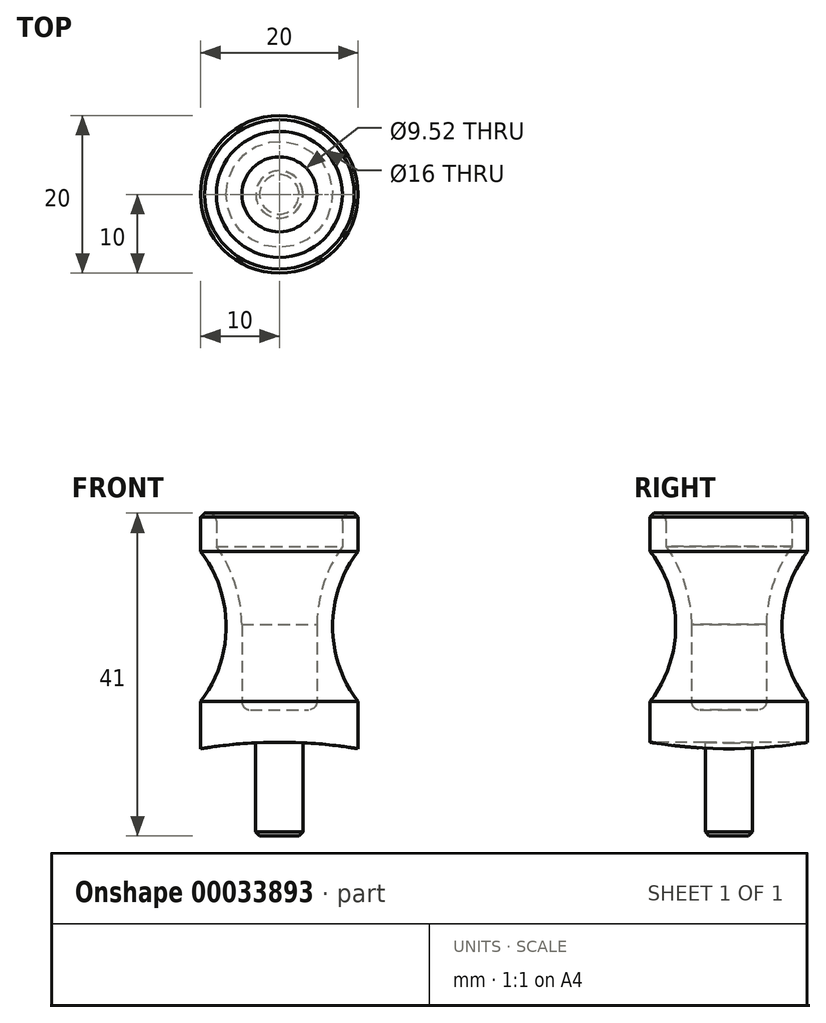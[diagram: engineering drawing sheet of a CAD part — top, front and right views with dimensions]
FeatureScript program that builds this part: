
annotation { "Feature Type Name" : "Feature", "Feature Type Description" : "" }
export const myFeature = defineFeature(function(context is Context, id is Id, definition is map)
    precondition{}
    {
        {
            var Q0;
            Q0=qCreatedBy(makeId("Front.planeOp"),FACE);
            var sketch = newSketch(context, id + "F0", { "sketchPlane" : qUnion([Q0])});
            skLineSegment(sketch, "E0", {"start": v(0, 0.9) * mm, "end": v(0, 63.05) * mm});
            skLineSegment(sketch, "E1", {"start": v(0, 0) * mm, "end": v(-10, 0) * mm});
            skLineSegment(sketch, "E2.0", {"start": v(-9, 30) * mm, "end": v(-10, 30) * mm});
            skLineSegment(sketch, "E3.0", {"start": v(-10, 0) * mm, "end": v(-10, 6.06) * mm});
            skArc(sketch, "E4.trimOffspring", {"start": v(-10, 6.06) * mm, "mid": v(-6.76, 15.6) * mm, "end": v(-10, 25.13) * mm});
            skLineSegment(sketch, "E5.trimOffspring", {"start": v(-10, 25.13) * mm, "end": v(-10, 30) * mm});
            skLineSegment(sketch, "E6.0", {"start": v(-8, 25.79) * mm, "end": v(-8, 29) * mm});
            skArc(sketch, "E7.0", {"start": v(-4.76, 15.35) * mm, "mid": v(-5.55, 20.82) * mm, "end": v(-8, 25.79) * mm});
            skLineSegment(sketch, "E8.0", {"start": v(0, 5) * mm, "end": v(-3.7, 5) * mm});
            skLineSegment(sketch, "E9.0", {"start": v(0, -60) * mm, "end": v(-10, -60) * mm});
            skArc(sketch, "E10", {"start": v(10, 0.07) * mm, "mid": v(0, 0.9) * mm, "end": v(-10, 0.07) * mm});
            skLineSegment(sketch, "E11.MirrorCS", {"start": v(10, 0) * mm, "end": v(10, 6.06) * mm});
            skLineSegment(sketch, "E12", {"start": v(0, 0) * mm, "end": v(0, 0.9) * mm});
            skLineSegment(sketch, "E13", {"start": v(0, 0) * mm, "end": v(10, 0) * mm});
            skLineSegment(sketch, "E14", {"start": v(-4.76, 15.84) * mm, "end": v(-4.76, 6.07) * mm});
            skPoint(sketch, "E14.startSnap0", {"position": v(-4.76, 15.35) * mm});
            skPoint(sketch, "E15.visualSharp", {"position": v(-4.76, 5) * mm});
            skArc(sketch, "E15.filletArc", {"start": v(-4.76, 6.07) * mm, "mid": v(-4.45, 5.31) * mm, "end": v(-3.7, 5) * mm});
            skPoint(sketch, "E16.visualSharp", {"position": v(-8, 30) * mm});
            skArc(sketch, "E16.filletArc", {"start": v(-8, 29) * mm, "mid": v(-8.3, 29.7) * mm, "end": v(-9, 30) * mm});
            skSolve(sketch);
        }
        {
            var Q0;
            {var subQ1=sQuery(id+"F0.wireOp",EDGE,"E1");Q0=makeQuery(id+"F0.imprint","IMPRINT",FACE,{"disambiguationData":[TD([[makeQuery(id+"F0.imprint","IMPRINT",EDGE,{"derivedFrom":subQ1}),-1.0]])]});}
            var Q1;
            Q1=makeQuery(id+"F0.imprint","IMPRINT",FACE,{"disambiguationData":[TD([[makeQuery(id+"F0.imprint","IMPRINT",EDGE,{"derivedFrom":sQuery(id+"F0.wireOp",EDGE,"E2.0")}),1.0]])]});
            var Q2;
            Q2=sQuery(id+"F0.wireOp",EDGE,"E10");
            var Q3;
            Q3=sQuery(id+"F0.wireOp",EDGE,"E0");
            revolve(context, id + "F1", {"entities" : qUnion([Q0, Q1]), "surfaceEntities" : qUnion([Q2]), "axis" : qUnion([Q3]), "revolveType" : RevolveType.FULL});
        }
        {
            var Q0;
            {var subQ4=sQuery(id+"F0.wireOp",EDGE,"E1");Q0=makeQuery(id+"F0.imprint","IMPRINT",FACE,{"disambiguationData":[TD([[makeQuery(id+"F0.imprint","IMPRINT",EDGE,{"derivedFrom":subQ4}),-1.0]])]});}
            var Q1;
            {var subQ1=sQuery(id+"F0.wireOp",EDGE,"E12");Q1=makeQuery(id+"F0.imprint","IMPRINT",FACE,{"disambiguationData":[TD([[makeQuery(id+"F0.imprint","IMPRINT",EDGE,{"derivedFrom":subQ1}),-1.0]])]});}
            extrude(context, id + "F2", {"entities" : qUnion([Q0, Q1]), "operationType" : NewBodyOperationType.REMOVE, "endBound" : BoundingType.SYMMETRIC, "oppositeDirection" : true, "depth" : 25 * mm});
        }
        {
            var Q0;
            Q0=makeQuery(id+"F1.opRevolve","SWEPT_FACE",FACE,{"disambiguationData":[OSD([sQuery(id+"F0.wireOp",EDGE,"E8.0")])]});
            var sketch = newSketch(context, id + "F3", { "sketchPlane" : qUnion([Q0])});
            skCircle(sketch, "E17", {"center": v(0, 0) * mm, "radius": 3 * mm});
            skSolve(sketch);
        }
        {
            var Q0;
            Q0 = qSketchRegion(id + "F3", true);
            extrude(context, id + "F4", {"entities" : qUnion([Q0]), "operationType" : NewBodyOperationType.ADD, "oppositeDirection" : true, "depth" : 16 * mm});
        }
        {
            var Q0;
            Q0=makeQuery(id+"F1.opRevolve","SWEPT_EDGE",EDGE,{"disambiguationData":[OSD([sQuery(id+"F0.wireOp",EDGE,"E2.0"),sQuery(id+"F0.wireOp",EDGE,"E5.trimOffspring")])]});
            chamfer(context, id + "F5", {"entities" : qUnion([Q0]), "width" : 0.5 * mm, "tangentPropagation" : true});
        }
        {
            var Q0;
            Q0=makeQuery(id+"F4.opExtrude","CAP_EDGE",EDGE,{"disambiguationData":[OSD([sQuery(id+"F3.wireOp",EDGE,"E17")])],"isStart":false});
            chamfer(context, id + "F6", {"entities" : qUnion([Q0]), "width" : 0.5 * mm, "tangentPropagation" : true});
        }
    });
